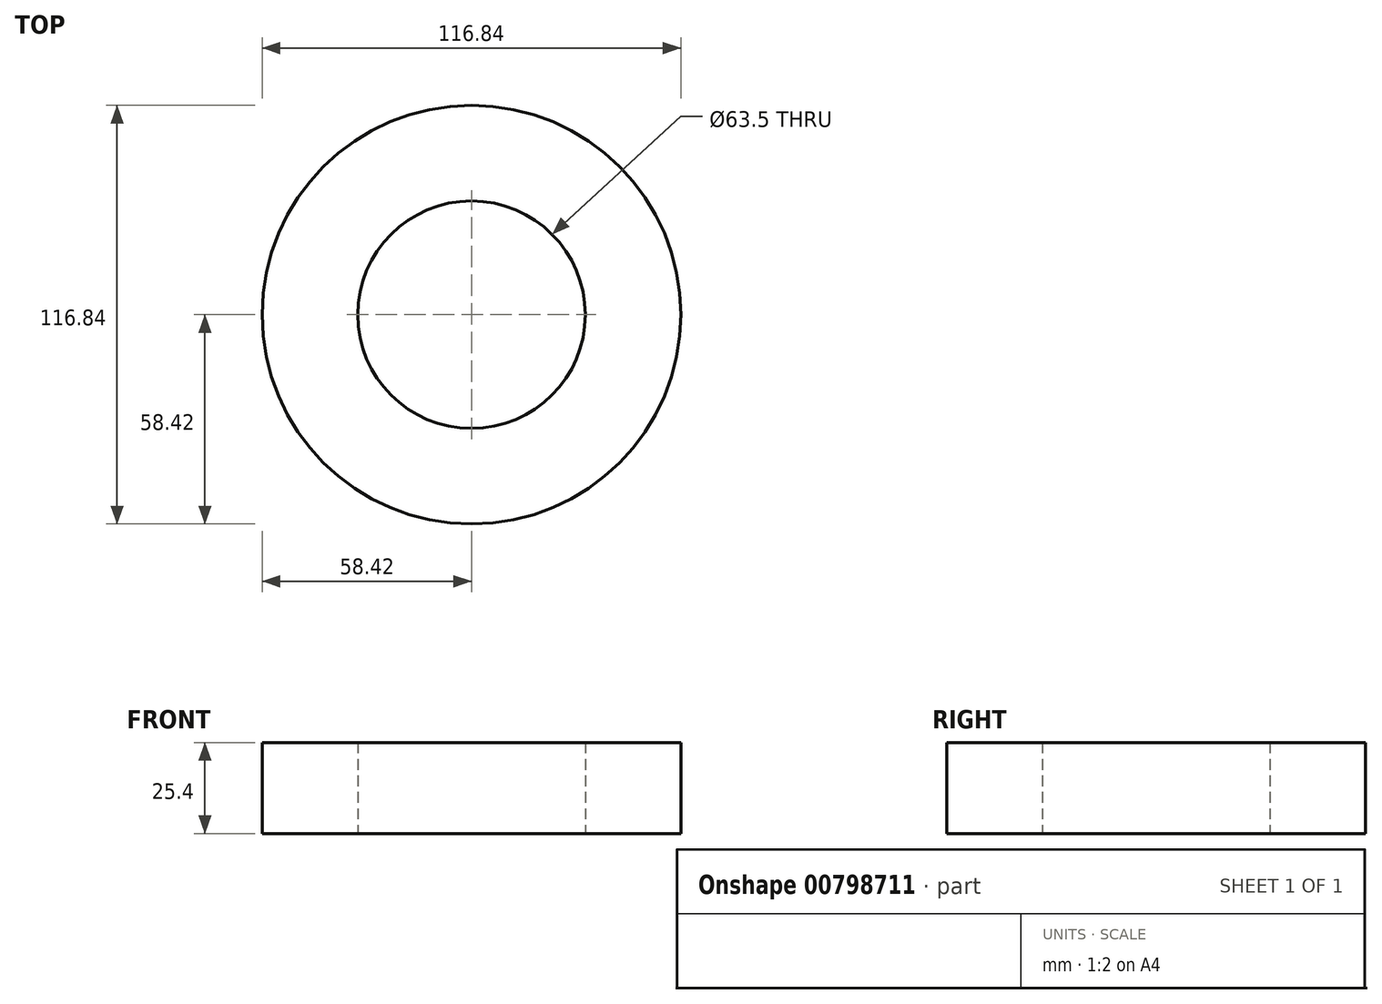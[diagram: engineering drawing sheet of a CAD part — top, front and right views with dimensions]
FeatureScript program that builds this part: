
annotation { "Feature Type Name" : "Feature", "Feature Type Description" : "" }
export const myFeature = defineFeature(function(context is Context, id is Id, definition is map)
    precondition{}
    {
        {
            var Q0;
            Q0=qCreatedBy(makeId("Top.planeOp"),FACE);
            var sketch = newSketch(context, id + "F0", { "sketchPlane" : qUnion([Q0])});
            skCircle(sketch, "E0", {"center": v(0, 0) * mm, "radius": 31.75 * mm});
            skCircle(sketch, "E1", {"center": v(0, 0) * mm, "radius": 58.42 * mm});
            skSolve(sketch);
        }
        {
            var Q0;
            Q0 = qSketchRegion(id + "F0", true);
            extrude(context, id + "F1", {"entities" : qUnion([Q0]), "depth" : 25.4 * mm, "offsetDistance" : 25.4 * mm});
        }
    });
